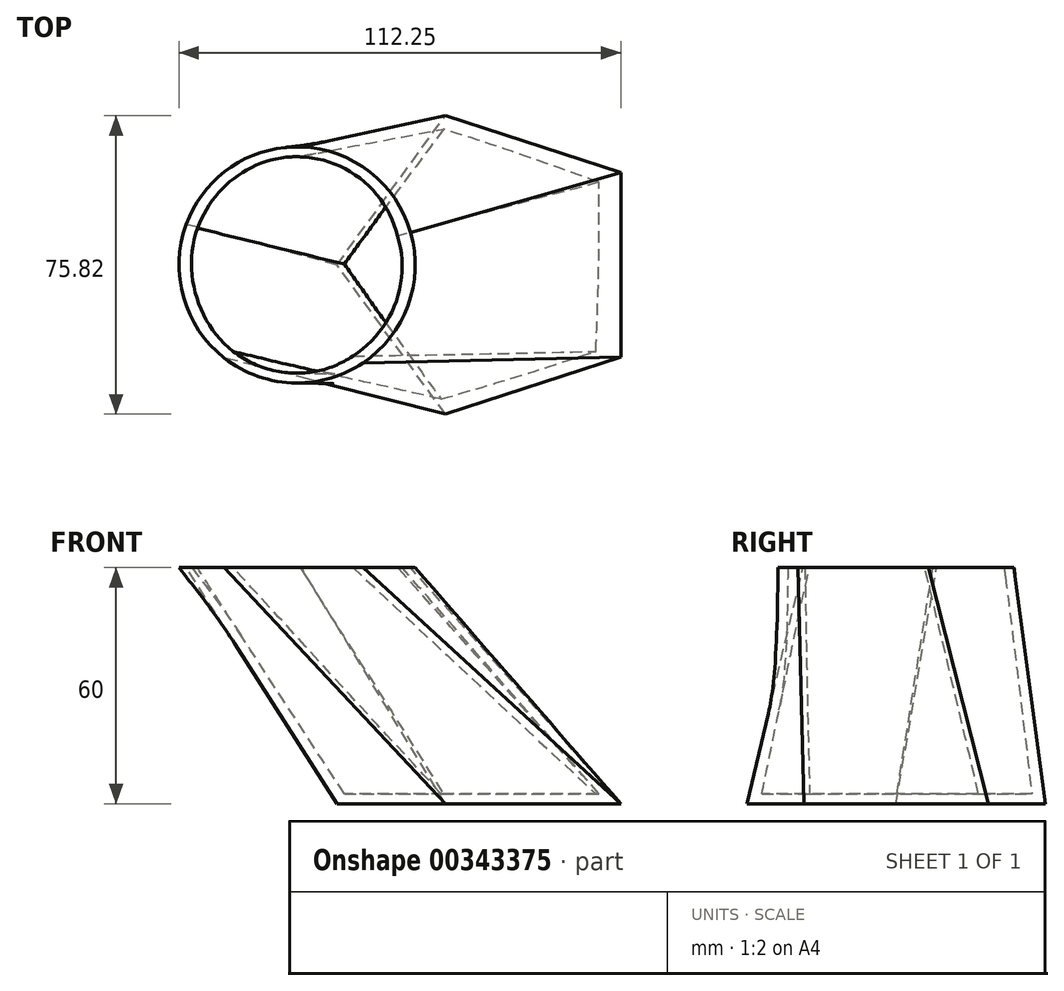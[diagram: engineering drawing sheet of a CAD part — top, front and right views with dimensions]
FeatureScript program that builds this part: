
annotation { "Feature Type Name" : "Feature", "Feature Type Description" : "" }
export const myFeature = defineFeature(function(context is Context, id is Id, definition is map)
    precondition{}
    {
        {
            var Q0;
            Q0=qCreatedBy(makeId("Top.planeOp"),FACE);
            var sketch = newSketch(context, id + "F0", { "sketchPlane" : qUnion([Q0])});
            skCircle(sketch, "E0.cCircle", {"center": v(0, 0) * mm, "radius": 32.25 * mm, "construction": true});
            skLineSegment(sketch, "E0.0", {"start": v(32.25, 23.43) * mm, "end": v(32.25, -23.43) * mm});
            skLineSegment(sketch, "E0.1", {"start": v(32.25, -23.43) * mm, "end": v(-12.32, -37.9) * mm});
            skLineSegment(sketch, "E0.2", {"start": v(-12.32, -37.9) * mm, "end": v(-39.86, 0) * mm});
            skLineSegment(sketch, "E0.3", {"start": v(-39.86, 0) * mm, "end": v(-12.32, 37.9) * mm});
            skLineSegment(sketch, "E0.4", {"start": v(-12.32, 37.9) * mm, "end": v(32.25, 23.43) * mm});
            skPoint(sketch, "E0.0.midPoint", {"position": v(32.25, 0) * mm});
            skSolve(sketch);
        }
        {
            var Q0;
            Q0=qCreatedBy(makeId("Top.planeOp"),FACE);
            cPlane(context, id + "F1", {"entities" : qUnion([Q0]), "cplaneType" : CPlaneType.OFFSET, "offset" : 60 * mm, "width" : 150 * mm, "height" : 150 * mm});
        }
        {
            var Q0;
            Q0=qCreatedBy(id+"F1.planeOp",FACE);
            var sketch = newSketch(context, id + "F2", { "sketchPlane" : qUnion([Q0])});
            skLineSegment(sketch, "E1", {"start": v(0, 0) * mm, "end": v(-50, 0) * mm, "construction": true});
            skCircle(sketch, "E2", {"center": v(-50, 0) * mm, "radius": 30 * mm});
            skSolve(sketch);
        }
        {
            var Q0;
            Q0=makeQuery(id+"F0.imprint","IMPRINT",FACE,{"disambiguationData":[TD([[makeQuery(id+"F0.imprint","IMPRINT",EDGE,{"derivedFrom":sQuery(id+"F0.wireOp",EDGE,"E0.0")}),-1.0]])]});
            var Q1;
            Q1=makeQuery(id+"F2.imprint","IMPRINT",FACE,{"disambiguationData":[TD([[makeQuery(id+"F2.imprint","IMPRINT",EDGE,{"derivedFrom":sQuery(id+"F2.wireOp",EDGE,"E2")}),1.0]])]});
            loft(context, id + "F3", {"sheetProfilesArray" : [{ "sheetProfileEntities" : qUnion([Q0]) }, { "sheetProfileEntities" : qUnion([Q1]) }]});
        }
        {
            var Q0;
            Q0=makeQuery(id+"F3.opLoft","CAP_FACE",FACE,{"disambiguationData":[OSD([makeQuery(id+"F2.imprint","IMPRINT",FACE,{"disambiguationData":[TD([[makeQuery(id+"F2.imprint","IMPRINT",EDGE,{"derivedFrom":sQuery(id+"F2.wireOp",EDGE,"E2")}),1.0]])]})])],"isStart":true});
            shell(context, id + "F4", {"entities" : qUnion([Q0]), "thickness" : 2.5 * mm});
        }
    });
